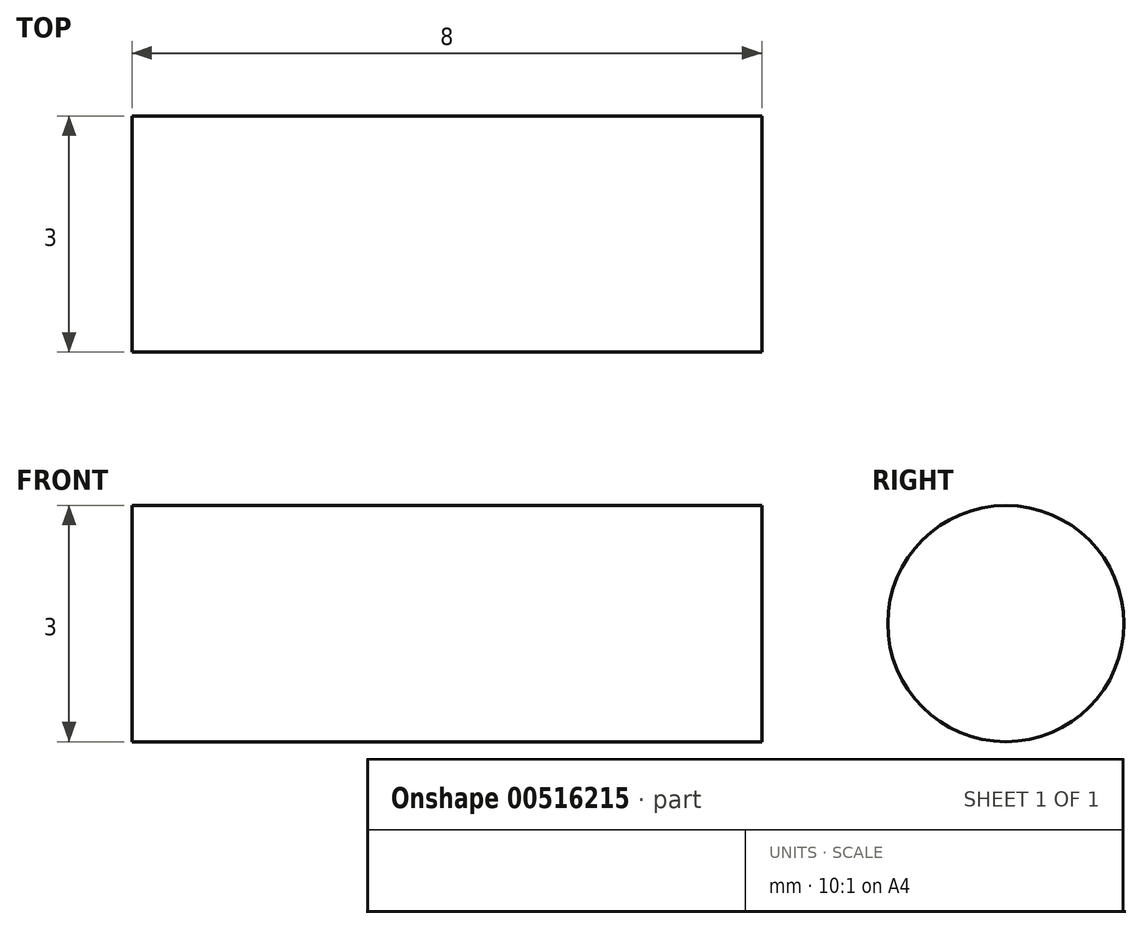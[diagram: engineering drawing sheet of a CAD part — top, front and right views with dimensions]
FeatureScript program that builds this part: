
annotation { "Feature Type Name" : "Feature", "Feature Type Description" : "" }
export const myFeature = defineFeature(function(context is Context, id is Id, definition is map)
    precondition{}
    {
        {
            var Q0;
            Q0=qCreatedBy(makeId("Right.planeOp"),FACE);
            var sketch = newSketch(context, id + "F0", { "sketchPlane" : qUnion([Q0])});
            skCircle(sketch, "E0", {"center": v(0, 0) * mm, "radius": 1.5 * mm});
            skSolve(sketch);
        }
        {
            var Q0;
            Q0=makeQuery(id+"F0.imprint","IMPRINT",FACE,{"disambiguationData":[TD([[makeQuery(id+"F0.imprint","IMPRINT",EDGE,{"derivedFrom":sQuery(id+"F0.wireOp",EDGE,"E0")}),1.0]])]});
            extrude(context, id + "F1", {"entities" : qUnion([Q0]), "depth" : 8 * mm, "offsetDistance" : 25 * mm});
        }
    });
